# Revit family: 1Baby_Changing_Station-Koala_Kare-KB300_Closed
name_source: partatom
category: Specialty Equipment
units: mm (PartAtom-declared; Revit-internal decimal feet)

## family parameters
Cut with Voids When Loaded = No
Host = Face
OmniClass Number = 23.40.20.21.37
OmniClass Title = Diaper Changing Units
Part Type = Normal
Room Calculation Point = No
Round Connector Dimension = Use Diameter
Shared = Yes

## types (3) — shared parameters
ADA Compliant = Yes
Assembly Code = C1030200
Braille Label = No
Default Elevation = 27"
Description = Baby Changing Station
Finish - Hook = Stainless Steel-Koala Kare-Polished
Height = 20 3/4"
Installation Type = Surface-Mounted
Length = 4"
Manufacturer = Koala Kare
Microban Antimicrobial Additive = Yes
Price = Prices may vary. Please consult Manufacturer Representative for most up-to-date price list.
URL = https://www.koalabear.com
Warranty Information = 5-year limited warranty on materials and workmanship and include a provision for replacement caused by vandalism
Width = 35 15/16"

## per-type parameters (varying)
| type | Material |
| KB300-00 | Polypropylene-Koala Kare-Beige |
| KB300-01 | Polypropylene-Koala Kare-Grey |
| KB300-05 | Polypropylene-Koala Kare-White Granite |

note: column(s) folded — value = type name in every type: Model

## geometry (parser evidence)
native form markers: Sweep x1
no freeform markers — native parametric forms only
